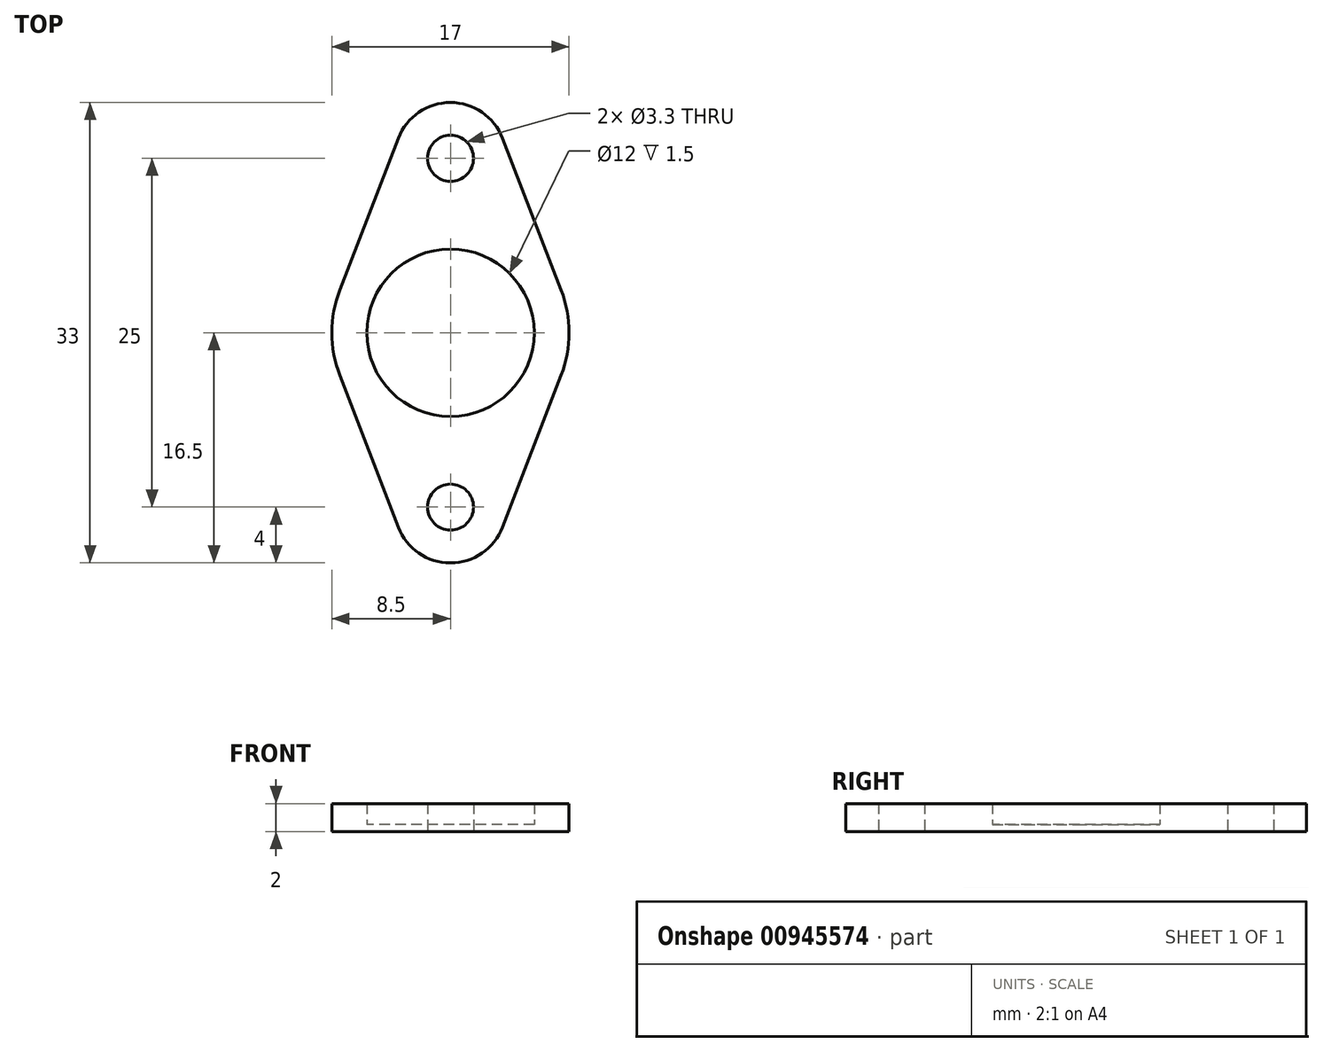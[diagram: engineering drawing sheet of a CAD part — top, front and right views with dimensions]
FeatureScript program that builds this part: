
annotation { "Feature Type Name" : "Feature", "Feature Type Description" : "" }
export const myFeature = defineFeature(function(context is Context, id is Id, definition is map)
    precondition{}
    {
        {
            var Q0;
            Q0=qCreatedBy(makeId("Top.planeOp"),FACE);
            var sketch = newSketch(context, id + "F0", { "sketchPlane" : qUnion([Q0])});
            skCircle(sketch, "E0", {"center": v(0, 0) * mm, "radius": 6 * mm});
            skArc(sketch, "E1", {"start": v(-7.93, 3.06) * mm, "mid": v(-8.5, 0) * mm, "end": v(-7.93, -3.06) * mm});
            skLineSegment(sketch, "E2", {"start": v(0, 12.5) * mm, "end": v(0, -12.5) * mm, "construction": true});
            skCircle(sketch, "E3", {"center": v(0, 12.5) * mm, "radius": 1.65 * mm});
            skCircle(sketch, "E4", {"center": v(0, -12.5) * mm, "radius": 1.65 * mm});
            skArc(sketch, "E5", {"start": v(3.73, 13.94) * mm, "mid": v(0, 16.5) * mm, "end": v(-3.73, 13.94) * mm});
            skArc(sketch, "E6", {"start": v(-3.73, -13.94) * mm, "mid": v(0, -16.5) * mm, "end": v(3.73, -13.94) * mm});
            skLineSegment(sketch, "E7", {"start": v(-3.73, 13.94) * mm, "end": v(-7.93, 3.06) * mm});
            skLineSegment(sketch, "E8", {"start": v(3.73, 13.94) * mm, "end": v(7.93, 3.06) * mm});
            skLineSegment(sketch, "E9", {"start": v(-7.93, -3.06) * mm, "end": v(-3.73, -13.94) * mm});
            skLineSegment(sketch, "E10", {"start": v(3.73, -13.94) * mm, "end": v(7.93, -3.06) * mm});
            skArc(sketch, "E11.trimOffspring", {"start": v(7.93, -3.06) * mm, "mid": v(8.5, 0) * mm, "end": v(7.93, 3.06) * mm});
            skSolve(sketch);
        }
        {
            var Q0;
            Q0=makeQuery(id+"F0.imprint","IMPRINT",FACE,{"disambiguationData":[TD([[makeQuery(id+"F0.imprint","IMPRINT",EDGE,{"derivedFrom":sQuery(id+"F0.wireOp",EDGE,"E0")}),-1.0]])]});
            extrude(context, id + "F1", {"entities" : qUnion([Q0]), "depth" : 2 * mm, "offsetDistance" : 25 * mm});
        }
        {
            var Q0;
            Q0=makeQuery(id+"F0.imprint","IMPRINT",FACE,{"disambiguationData":[TD([[makeQuery(id+"F0.imprint","IMPRINT",EDGE,{"derivedFrom":sQuery(id+"F0.wireOp",EDGE,"E0")}),1.0]])]});
            extrude(context, id + "F2", {"entities" : qUnion([Q0]), "operationType" : NewBodyOperationType.ADD, "depth" : 0.5 * mm, "offsetDistance" : 25 * mm});
        }
    });
